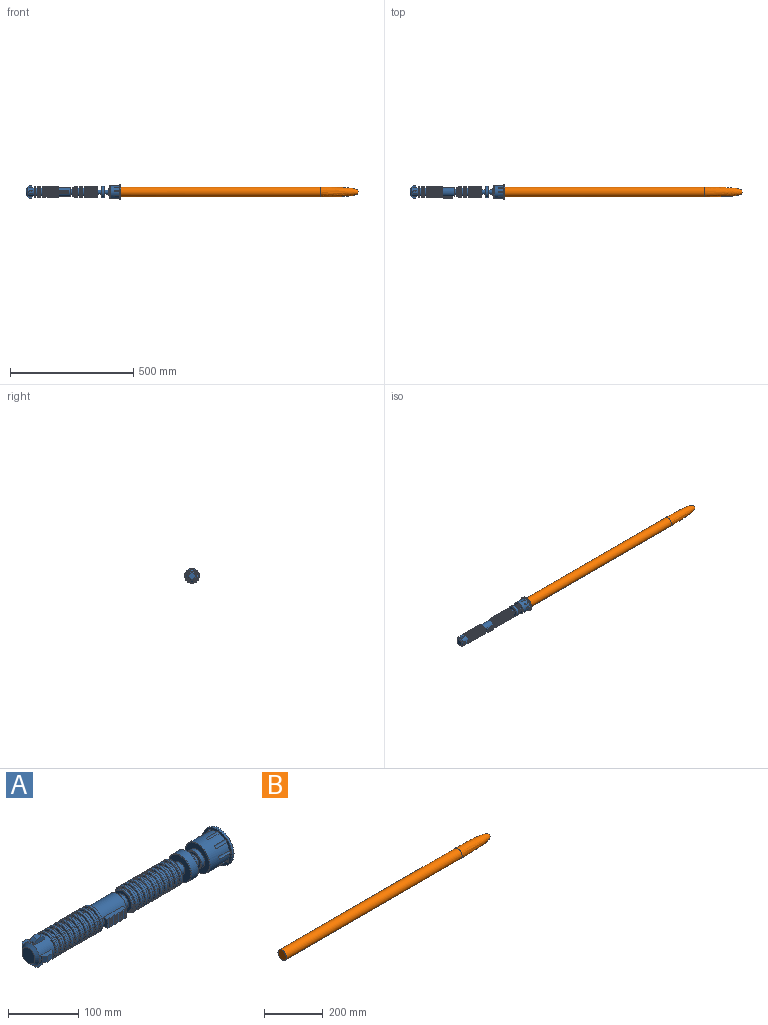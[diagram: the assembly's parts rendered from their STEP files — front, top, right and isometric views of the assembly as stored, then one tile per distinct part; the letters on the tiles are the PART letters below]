
ASSEMBLY  parts=2 mates=1
PART A: 231 faces, bbox 384x60x60 mm
  f0: plane 10x2.71mm, normal (-1,0,0), area 22.3mm2, adj f5,f6,f74,f81
  f1: plane 10x2.71mm, normal (-1,0,0), area 22.3mm2, adj f4,f6,f72,f85
  f2: plane 10x2.71mm, normal (1,0,0), area 22.3mm2, adj f5,f6,f74,f82
  f3: plane 10x2.71mm, normal (1,0,0), area 22.3mm2, adj f4,f6,f72,f86
  f4: plane 20x7.71mm, normal (0,-1,0), area 129.2mm2, adj f1,f3,f6,f73,f85,f86
  f5: plane 20x7.71mm, normal (0,-1,0), area 129.2mm2, adj f0,f2,f6,f75,f81,f82
  f6: cylinder r=18mm len=36mm, axis (-1,0,0), area 2582.3mm2, adj f0,f1,f2,f3,f4,f5,f11,f67
  f7: plane 40.5x40.5mm, normal (-1,0,0), area 270.4mm2, adj f8,f65
  f8: cylinder r=18mm len=36mm, axis (-1,0,0), area 565.5mm2, adj f7,f9
  f9: plane 40.5x40.5mm, normal (1,0,0), area 270.4mm2, adj f8,f46
  f10: cylinder r=21mm len=42mm, axis (-1,0,0), area 461.8mm2, adj f46,f47
  f11: plane 40.5x40.5mm, normal (-1,0,0), area 270.4mm2, adj f6,f47
  f12: plane 40.5x40.5mm, normal (1,0,0), area 270.4mm2, adj f48,f95
  f13: cylinder r=21mm len=42mm, axis (-1,0,0), area 461.8mm2, adj f48,f49
  f14: plane 40.5x40.5mm, normal (-1,0,0), area 270.4mm2, adj f15,f49
  f15: cylinder r=18mm len=36mm, axis (-1,0,0), area 565.5mm2, adj f14,f16
  f16: plane 40.5x40.5mm, normal (1,0,0), area 270.4mm2, adj f15,f50
  f17: cylinder r=21mm len=42mm, axis (-1,0,0), area 461.8mm2, adj f50,f51
  f18: plane 40.5x40.5mm, normal (-1,0,0), area 270.4mm2, adj f19,f51
  f19: cylinder r=18mm len=36mm, axis (-1,0,0), area 565.5mm2, adj f18,f20
  f20: plane 40.5x40.5mm, normal (1,0,0), area 270.4mm2, adj f19,f52
  f21: cylinder r=21mm len=42mm, axis (-1,0,0), area 461.8mm2, adj f52,f53
  f22: plane 40.5x40.5mm, normal (-1,0,0), area 270.4mm2, adj f23,f53
  f23: cylinder r=18mm len=36mm, axis (-1,0,0), area 565.5mm2, adj f22,f24
  f24: plane 40.5x40.5mm, normal (1,0,0), area 270.4mm2, adj f23,f54
  f25: cylinder r=21mm len=42mm, axis (-1,0,0), area 461.8mm2, adj f54,f55
  f26: plane 40.5x40.5mm, normal (-1,0,0), area 270.4mm2, adj f27,f55
  f27: cylinder r=18mm len=36mm, axis (-1,0,0), area 565.5mm2, adj f26,f28
  f28: plane 40.5x40.5mm, normal (1,0,0), area 270.4mm2, adj f27,f56
  f29: cylinder r=21mm len=42mm, axis (-1,0,0), area 461.8mm2, adj f56,f57
  f30: plane 40.5x40.5mm, normal (-1,0,0), area 270.4mm2, adj f31,f57
  f31: cylinder r=18mm len=36mm, axis (-1,0,0), area 565.5mm2, adj f30,f32
  f32: plane 40.5x40.5mm, normal (1,0,0), area 270.4mm2, adj f31,f58
  f33: cylinder r=21mm len=42mm, axis (-1,0,0), area 461.8mm2, adj f58,f59
  f34: plane 40.5x40.5mm, normal (-1,0,0), area 270.4mm2, adj f35,f59
  f35: cylinder r=18mm len=36mm, axis (-1,0,0), area 565.5mm2, adj f34,f36
  f36: plane 40.5x40.5mm, normal (1,0,0), area 270.4mm2, adj f35,f60
  f37: cylinder r=21mm len=42mm, axis (-1,0,0), area 461.8mm2, adj f60,f61
  f38: plane 40.5x40.5mm, normal (-1,0,0), area 270.4mm2, adj f39,f61
  f39: cylinder r=18mm len=36mm, axis (-1,0,0), area 565.5mm2, adj f38,f40
  f40: plane 40.5x40.5mm, normal (1,0,0), area 270.4mm2, adj f39,f62
  f41: cylinder r=21mm len=42mm, axis (-1,0,0), area 461.8mm2, adj f62,f63
  f42: plane 40.5x40.5mm, normal (-1,0,0), area 270.4mm2, adj f43,f63
  f43: cylinder r=18mm len=36mm, axis (-1,0,0), area 565.5mm2, adj f42,f44
  f44: plane 40.5x40.5mm, normal (1,0,0), area 270.4mm2, adj f43,f64
  f45: cylinder r=21mm len=42mm, axis (-1,0,0), area 461.8mm2, adj f64,f65
  f46: torus R=20.25mm, axis (-1,0,0), area 153.4mm2, adj f9,f10
  f47: torus R=20.25mm, axis (-1,0,0), area 153.4mm2, adj f10,f11
  f48: torus R=20.25mm, axis (-1,0,0), area 153.4mm2, adj f12,f13
  f49: torus R=20.25mm, axis (-1,0,0), area 153.4mm2, adj f13,f14
  f50: torus R=20.25mm, axis (-1,0,0), area 153.4mm2, adj f16,f17
  f51: torus R=20.25mm, axis (-1,0,0), area 153.4mm2, adj f17,f18
  f52: torus R=20.25mm, axis (-1,0,0), area 153.4mm2, adj f20,f21
  f53: torus R=20.25mm, axis (-1,0,0), area 153.4mm2, adj f21,f22
  f54: torus R=20.25mm, axis (-1,0,0), area 153.4mm2, adj f24,f25
  f55: torus R=20.25mm, axis (-1,0,0), area 153.4mm2, adj f25,f26
  f56: torus R=20.25mm, axis (-1,0,0), area 153.4mm2, adj f28,f29
  f57: torus R=20.25mm, axis (-1,0,0), area 153.4mm2, adj f29,f30
  f58: torus R=20.25mm, axis (-1,0,0), area 153.4mm2, adj f32,f33
  f59: torus R=20.25mm, axis (-1,0,0), area 153.4mm2, adj f33,f34
  f60: torus R=20.25mm, axis (-1,0,0), area 153.4mm2, adj f36,f37
  f61: torus R=20.25mm, axis (-1,0,0), area 153.4mm2, adj f37,f38
  f62: torus R=20.25mm, axis (-1,0,0), area 153.4mm2, adj f40,f41
  f63: torus R=20.25mm, axis (-1,0,0), area 153.4mm2, adj f41,f42
  f64: torus R=20.25mm, axis (-1,0,0), area 153.4mm2, adj f44,f45
  f65: torus R=20.25mm, axis (-1,0,0), area 153.4mm2, adj f7,f45
  f66: plane 26x26mm, normal (-1,0,0), area 530.9mm2, adj f89
  f67: plane 20x7.71mm, normal (0,0,-1), area 129.2mm2, adj f6,f68,f70,f71,f83,f84
  f68: plane 10x2.71mm, normal (1,0,0), area 22.3mm2, adj f6,f67,f69,f84
  f69: plane 20x7.71mm, normal (0,0,1), area 129.2mm2, adj f6,f68,f70,f71,f83,f84
  f70: plane 10x2.71mm, normal (-1,0,0), area 22.3mm2, adj f6,f67,f69,f83
  f71: plane 10x10mm, normal (0,1,0), area 100mm2, adj f67,f69,f83,f84
  f72: plane 20x7.71mm, normal (0,1,0), area 129.2mm2, adj f1,f3,f6,f73,f85,f86
  f73: plane 10x10mm, normal (0,0,-1), area 100mm2, adj f4,f72,f85,f86
  f74: plane 20x7.71mm, normal (0,1,0), area 129.2mm2, adj f0,f2,f6,f75,f81,f82
  f75: plane 10x10mm, normal (0,0,1), area 100mm2, adj f5,f74,f81,f82
  f76: plane 10x10mm, normal (0,-1,0), area 100mm2, adj f77,f79,f87,f88
  f77: plane 20x7.71mm, normal (0,0,-1), area 129.2mm2, adj f6,f76,f78,f80,f87,f88
  f78: plane 10x2.71mm, normal (1,0,0), area 22.3mm2, adj f6,f77,f79,f87
  f79: plane 20x7.71mm, normal (0,0,1), area 129.2mm2, adj f6,f76,f78,f80,f87,f88
  f80: plane 10x2.71mm, normal (-1,0,0), area 22.3mm2, adj f6,f77,f79,f88
  f81: plane 10x5mm, normal (-0.71,0,0.71), area 70.7mm2, adj f0,f5,f74,f75
  f82: plane 10x5mm, normal (0.71,0,0.71), area 70.7mm2, adj f2,f5,f74,f75
  f83: plane 10x5mm, normal (-0.71,0.71,0), area 70.7mm2, adj f67,f69,f70,f71
  f84: plane 10x5mm, normal (0.71,0.71,0), area 70.7mm2, adj f67,f68,f69,f71
  f85: plane 10x5mm, normal (-0.71,0,-0.71), area 70.7mm2, adj f1,f4,f72,f73
  f86: plane 10x5mm, normal (0.71,0,-0.71), area 70.7mm2, adj f3,f4,f72,f73
  f87: plane 10x5mm, normal (0.71,-0.71,0), area 70.7mm2, adj f76,f77,f78,f79
  f88: plane 10x5mm, normal (-0.71,-0.71,0), area 70.7mm2, adj f76,f77,f79,f80
  f89: cone r=13mm half-angle=45deg, axis (1,0,0), area 688.6mm2, adj f6,f66
  f90: plane 15x1.5mm, normal (1,0,0), area 22.5mm2, adj f92,f93,f94,f219
  f91: plane 15x1.5mm, normal (-1,0,0), area 22.5mm2, adj f92,f93,f94,f222
  f92: plane 38x8.64mm, normal (0,0,1), area 307.2mm2, adj f90,f91,f94,f95,f96,f97,f98,f99
  f93: plane 38x8.64mm, normal (0,0,-1), area 307.2mm2, adj f90,f91,f94,f95,f96,f97,f98,f99
  f94: plane 15x3mm, normal (0,-1,0), area 45mm2, adj f90,f91,f92,f93
  f95: cylinder r=18mm len=49.25mm, axis (-1,0,0), area 4982.1mm2, adj f12,f92,f93,f108,f112,f216
  f96: plane 15x1.5mm, normal (1,0,0), area 22.5mm2, adj f92,f93,f98,f220
  f97: plane 15x1.5mm, normal (-1,0,0), area 22.5mm2, adj f92,f93,f98,f218
  f98: plane 15x3mm, normal (0,-1,0), area 45mm2, adj f92,f93,f96,f97
  f99: plane 15x1.5mm, normal (-1,0,0), area 22.5mm2, adj f92,f93,f104,f225
  f100: plane 15x1.5mm, normal (1,0,0), area 22.5mm2, adj f92,f93,f217,f225
  f101: plane 15x1.5mm, normal (-1,0,0), area 22.5mm2, adj f92,f93,f217,f224
  f102: plane 15x1.5mm, normal (1,0,0), area 22.5mm2, adj f92,f93,f109,f224
  f103: plane 15x1.5mm, normal (1,0,0), area 22.5mm2, adj f92,f93,f104,f223
  f104: plane 15x3mm, normal (0,-1,0), area 45mm2, adj f92,f93,f99,f103
  f105: plane 15x1.5mm, normal (1,0,0), area 22.5mm2, adj f92,f93,f107,f218
  f106: plane 15x1.5mm, normal (-1,0,0), area 22.5mm2, adj f92,f93,f107,f219
  f107: plane 15x3mm, normal (0,-1,0), area 45mm2, adj f92,f93,f105,f106
  f108: plane 15x8.64mm, normal (-1,0,0), area 113mm2, adj f92,f93,f95,f109
  f109: plane 15x3mm, normal (0,-1,0), area 45mm2, adj f92,f93,f102,f108
  f110: plane 15x1.5mm, normal (-1,0,0), area 22.5mm2, adj f92,f93,f221,f223
  f111: plane 15x1.5mm, normal (1,0,0), area 22.5mm2, adj f92,f93,f221,f222
  f112: plane 15x8.64mm, normal (1,0,0), area 113mm2, adj f92,f93,f95,f114
  f113: plane 15x1.5mm, normal (-1,0,0), area 22.5mm2, adj f92,f93,f114,f220
  f114: plane 15x3mm, normal (0,-1,0), area 45mm2, adj f92,f93,f112,f113
  f115: cylinder r=25mm len=50mm, axis (-1,0,0), area 5220mm2, adj f119,f122,f123,f124,f125,f126,f127,f128
  f116: plane 48.5x48.5mm, normal (-1,0,0), area 1140.6mm2, adj f122,f147
  f117: cylinder r=30mm len=60mm, axis (-1,0,0), area 754mm2, adj f118,f119
  f118: plane 60x60mm, normal (1,0,0), area 1394.1mm2, adj f117,f120,f124,f126,f128,f130,f132,f134
  f119: plane 60x60mm, normal (-1,0,0), area 773.8mm2, adj f115,f117,f124,f126,f128,f130,f132,f134
  f120: cylinder r=20mm len=40mm, axis (-1,0,0), area 4900.9mm2, adj f118,f121
  f121: plane 40x40mm, normal (1,0,0), area 1256.6mm2, adj f120
  f122: torus R=24.25mm, axis (1,0,0), area 183mm2, adj f115,f116
  f123: plane 4.52x3.76mm, normal (1,0,0), area 9.6mm2, adj f115,f124
  f124: cylinder r=2.5mm len=25mm, axis (1,0,0), area 222.6mm2, adj f115,f118,f119,f123
  f125: plane 4.85x3.11mm, normal (1,0,0), area 9.6mm2, adj f115,f126
  f126: cylinder r=2.5mm len=25mm, axis (1,0,0), area 222.6mm2, adj f115,f118,f119,f125
  f127: plane 4.75x3.37mm, normal (1,0,0), area 9.6mm2, adj f115,f128
  f128: cylinder r=2.5mm len=25mm, axis (1,0,0), area 222.6mm2, adj f115,f118,f119,f127
  f129: plane 4.67x3.52mm, normal (1,0,0), area 9.6mm2, adj f115,f130
  f130: cylinder r=2.5mm len=25mm, axis (1,0,0), area 222.6mm2, adj f115,f118,f119,f129
  f131: plane 4.9x2.95mm, normal (1,0,0), area 9.6mm2, adj f115,f132
  f132: cylinder r=2.5mm len=25mm, axis (1,0,0), area 222.6mm2, adj f115,f118,f119,f131
  f133: plane 4.42x3.9mm, normal (1,0,0), area 9.6mm2, adj f115,f134
  f134: cylinder r=2.5mm len=25mm, axis (1,0,0), area 222.6mm2, adj f115,f118,f119,f133
  f135: plane 4.99x2.54mm, normal (1,0,0), area 9.6mm2, adj f115,f136
  f136: cylinder r=2.5mm len=25mm, axis (1,0,0), area 222.6mm2, adj f115,f118,f119,f135
  f137: plane 4.24x4.12mm, normal (1,0,0), area 9.6mm2, adj f115,f138
  f138: cylinder r=2.5mm len=25mm, axis (1,0,0), area 222.6mm2, adj f115,f118,f119,f137
  f139: plane 4.96x2.67mm, normal (1,0,0), area 9.6mm2, adj f115,f140
  f140: cylinder r=2.5mm len=25mm, axis (1,0,0), area 222.6mm2, adj f115,f118,f119,f139
  f141: plane 40.5x40.5mm, normal (1,0,0), area 974.1mm2, adj f142,f210
  f142: cylinder r=10mm len=20mm, axis (-1,0,0), area 942.5mm2, adj f141,f145
  f143: cylinder r=22.5mm len=45mm, axis (-1,0,0), area 1908.5mm2, adj f213,f214
  f144: plane 43.5x43.5mm, normal (1,0,0), area 1172mm2, adj f146,f214
  f145: plane 43.5x43.5mm, normal (-1,0,0), area 1172mm2, adj f142,f213
  f146: cylinder r=10mm len=20mm, axis (-1,0,0), area 785.4mm2, adj f144,f148
  f147: cylinder r=15mm len=30mm, axis (-1,0,0), area 636.2mm2, adj f116,f212
  f148: plane 28.5x28.5mm, normal (-1,0,0), area 323.8mm2, adj f146,f212
  f149: plane 40.5x40.5mm, normal (-1,0,0), area 270.4mm2, adj f190,f211
  f150: plane 40.5x40.5mm, normal (1,0,0), area 270.4mm2, adj f190,f191
  f151: cylinder r=21mm len=42mm, axis (-1,0,0), area 461.8mm2, adj f191,f192
  f152: plane 40.5x40.5mm, normal (-1,0,0), area 270.4mm2, adj f189,f192
  f153: plane 40.5x40.5mm, normal (1,0,0), area 270.4mm2, adj f189,f193
  f154: cylinder r=21mm len=42mm, axis (-1,0,0), area 461.8mm2, adj f193,f194
  f155: plane 40.5x40.5mm, normal (-1,0,0), area 270.4mm2, adj f188,f194
  f156: plane 40.5x40.5mm, normal (1,0,0), area 270.4mm2, adj f188,f195
  f157: cylinder r=21mm len=42mm, axis (-1,0,0), area 461.8mm2, adj f195,f196
  f158: plane 40.5x40.5mm, normal (-1,0,0), area 270.4mm2, adj f187,f196
  f159: plane 40.5x40.5mm, normal (1,0,0), area 270.4mm2, adj f187,f197
  f160: cylinder r=21mm len=42mm, axis (-1,0,0), area 461.8mm2, adj f197,f198
  f161: plane 40.5x40.5mm, normal (-1,0,0), area 270.4mm2, adj f186,f198
  f162: plane 40.5x40.5mm, normal (1,0,0), area 270.4mm2, adj f186,f199
  f163: cylinder r=21mm len=42mm, axis (-1,0,0), area 461.8mm2, adj f199,f200
  f164: plane 40.5x40.5mm, normal (-1,0,0), area 270.4mm2, adj f185,f200
  f165: plane 40.5x40.5mm, normal (1,0,0), area 270.4mm2, adj f185,f201
  f166: cylinder r=21mm len=42mm, axis (-1,0,0), area 461.8mm2, adj f201,f202
  f167: plane 40.5x40.5mm, normal (-1,0,0), area 270.4mm2, adj f184,f202
  f168: plane 40.5x40.5mm, normal (1,0,0), area 270.4mm2, adj f184,f203
  f169: cylinder r=21mm len=42mm, axis (-1,0,0), area 461.8mm2, adj f203,f204
  f170: plane 40.5x40.5mm, normal (-1,0,0), area 270.4mm2, adj f183,f204
  f171: plane 40.5x40.5mm, normal (1,0,0), area 270.4mm2, adj f183,f205
  f172: cylinder r=21mm len=42mm, axis (-1,0,0), area 461.8mm2, adj f205,f206
  f173: plane 40.5x40.5mm, normal (-1,0,0), area 270.4mm2, adj f182,f206
  f174: plane 40.5x40.5mm, normal (1,0,0), area 270.4mm2, adj f182,f207
  f175: cylinder r=21mm len=42mm, axis (-1,0,0), area 461.8mm2, adj f207,f208
  f176: plane 40.5x40.5mm, normal (-1,0,0), area 183.8mm2, adj f208,f209
  f177: cylinder r=21mm len=42mm, axis (-1,0,0), area 461.8mm2, adj f210,f211
  f178: plane 34.5x34.5mm, normal (1,0,0), area 534.4mm2, adj f180,f216
  f179: cylinder r=18mm len=36mm, axis (-1,0,0), area 395.8mm2, adj f209,f215
  f180: cylinder r=11.29mm len=22.58mm, axis (-1,0,0), area 709.4mm2, adj f178,f181
  f181: plane 34.5x34.5mm, normal (-1,0,0), area 534.4mm2, adj f180,f215
  f182: cylinder r=18mm len=36mm, axis (-1,0,0), area 565.5mm2, adj f173,f174
  f183: cylinder r=18mm len=36mm, axis (-1,0,0), area 565.5mm2, adj f170,f171
  f184: cylinder r=18mm len=36mm, axis (-1,0,0), area 565.5mm2, adj f167,f168
  f185: cylinder r=18mm len=36mm, axis (-1,0,0), area 565.5mm2, adj f164,f165
  f186: cylinder r=18mm len=36mm, axis (-1,0,0), area 565.5mm2, adj f161,f162
  f187: cylinder r=18mm len=36mm, axis (-1,0,0), area 565.5mm2, adj f158,f159
  f188: cylinder r=18mm len=36mm, axis (-1,0,0), area 565.5mm2, adj f155,f156
  f189: cylinder r=18mm len=36mm, axis (-1,0,0), area 565.5mm2, adj f152,f153
  f190: cylinder r=18mm len=36mm, axis (-1,0,0), area 565.5mm2, adj f149,f150
  f191: torus R=20.25mm, axis (-1,0,0), area 153.4mm2, adj f150,f151
  f192: torus R=20.25mm, axis (-1,0,0), area 153.4mm2, adj f151,f152
  f193: torus R=20.25mm, axis (-1,0,0), area 153.4mm2, adj f153,f154
  f194: torus R=20.25mm, axis (-1,0,0), area 153.4mm2, adj f154,f155
  f195: torus R=20.25mm, axis (-1,0,0), area 153.4mm2, adj f156,f157
  f196: torus R=20.25mm, axis (-1,0,0), area 153.4mm2, adj f157,f158
  f197: torus R=20.25mm, axis (-1,0,0), area 153.4mm2, adj f159,f160
  f198: torus R=20.25mm, axis (-1,0,0), area 153.4mm2, adj f160,f161
  f199: torus R=20.25mm, axis (-1,0,0), area 153.4mm2, adj f162,f163
  f200: torus R=20.25mm, axis (-1,0,0), area 153.4mm2, adj f163,f164
  f201: torus R=20.25mm, axis (-1,0,0), area 153.4mm2, adj f165,f166
  f202: torus R=20.25mm, axis (-1,0,0), area 153.4mm2, adj f166,f167
  f203: torus R=20.25mm, axis (-1,0,0), area 153.4mm2, adj f168,f169
  f204: torus R=20.25mm, axis (-1,0,0), area 153.4mm2, adj f169,f170
  f205: torus R=20.25mm, axis (-1,0,0), area 153.4mm2, adj f171,f172
  f206: torus R=20.25mm, axis (-1,0,0), area 153.4mm2, adj f172,f173
  f207: torus R=20.25mm, axis (-1,0,0), area 153.4mm2, adj f174,f175
  f208: torus R=20.25mm, axis (-1,0,0), area 153.4mm2, adj f175,f176
  f209: torus R=18.75mm, axis (-1,0,0), area 135.3mm2, adj f176,f179
  f210: torus R=20.25mm, axis (1,0,0), area 153.4mm2, adj f141,f177
  f211: torus R=20.25mm, axis (-1,0,0), area 153.4mm2, adj f149,f177
  f212: torus R=14.25mm, axis (1,0,0), area 109mm2, adj f147,f148
  f213: torus R=21.75mm, axis (1,0,0), area 164.5mm2, adj f143,f145
  f214: torus R=21.75mm, axis (1,0,0), area 164.5mm2, adj f143,f144
  f215: torus R=17.25mm, axis (1,0,0), area 131.2mm2, adj f179,f181
  f216: torus R=17.25mm, axis (1,0,0), area 131.2mm2, adj f95,f178
  f217: plane 15x3mm, normal (0,-1,0), area 45mm2, adj f92,f93,f100,f101
  f218: plane 15x2mm, normal (0,-1,0), area 30mm2, adj f92,f93,f97,f105
  f219: plane 15x2mm, normal (0,-1,0), area 30mm2, adj f90,f92,f93,f106
  f220: plane 15x2mm, normal (0,-1,0), area 30mm2, adj f92,f93,f96,f113
  f221: plane 15x3mm, normal (0,-1,0), area 45mm2, adj f92,f93,f110,f111
  f222: plane 15x2mm, normal (0,-1,0), area 30mm2, adj f91,f92,f93,f111
  f223: plane 15x2mm, normal (0,-1,0), area 30mm2, adj f92,f93,f103,f110
  f224: plane 15x2mm, normal (0,-1,0), area 30mm2, adj f92,f93,f101,f102
  f225: plane 15x2mm, normal (0,-1,0), area 30mm2, adj f92,f93,f99,f100
  f226: cylinder r=7.5mm len=40mm, axis (-1,0,0), area 989.6mm2, adj f227,f228,f229,f230
  f227: plane 15x7.5mm, normal (1,0,0), area 88.4mm2, adj f226,f230
  f228: plane 15x15mm, normal (-1,0,0), area 176.7mm2, adj f226
  f229: plane 15x7.5mm, normal (1,0,0), area 88.4mm2, adj f226,f230
  f230: plane 38x15mm, normal (0,1,0), area 570mm2, adj f226,f227,f229
PART B: 3 faces, bbox 1000x40x40 mm
  f0: plane 40x40mm, normal (-1,0,0), area 1256.6mm2, adj f1
  f1: cylinder r=20mm len=850mm, axis (-1,0,0), area 106814.2mm2, adj f0,f2
  f2: revolved ~150x40mm, area 16721.2mm2, adj f1
PLACE A t=(-154.47,25.69,-11.97)mm
PLACE B t=(198.03,-58.21,6.03)mm
MATE planar B.f1 <-> A.f95  axis (-1,0,0) through (160.53,25.69,6.03)mm
